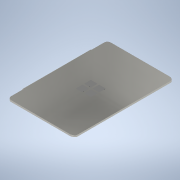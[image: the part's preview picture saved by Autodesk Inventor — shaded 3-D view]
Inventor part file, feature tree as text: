
AUTODESK INVENTOR PART (.ipt)
format: ipt  version: 2022 (Build 260153000, 153)  size: 223,744 bytes
history: native  units: mm
features: extrude x6, sketch x4, plane x1, direct_edit x1, other x1
ambient origin geometry x8: Origin, YZ Plane, XZ Plane, XY Plane, X Axis, Y Axis, Z Axis, Center Point
bodies: Body1 (feature_tree)
feature tree (13):
  plane  "Work Plane1"
  sketch  "Sketch2"  dims[d7=0.5mm d8=0.0mm d9=0.49mm d10=0.0mm]
  extrude  "Extrusion2"  Depth=0.5mm TaperAngle=0.0deg
  extrude  "Extrusion3"  Depth=2.0mm
  extrude  "Extrusion4"  Depth=0.5mm
  extrude  "Extrusion5"  Depth=10.0mm
  extrude  "Extrusion6"  Depth=10.0mm
  extrude  "Extrusion7"  Depth=10.0mm TaperAngle=0.0deg
  direct_edit  "Direct Edit1"
  sketch  "Sketch3"  dims[d11=2.0mm d12=2.0mm]
  sketch  "Sketch4"  dims[d13=0.5mm d14=0.5mm]
  sketch  "Sketch6"  dims[d15=0.5mm d16=12.75mm d17=7.75mm d18=0.001mm d19=0.0mm d20=0.25mm d21=0.315mm d22=15.0mm d23=0.001mm d24=0.0mm d26=0.0mm d32=21.5mm d33=0.0mm d34=20.425mm d35=0.0mm d36=0.5mm d37=5.0mm d38=10.0mm d39=10.0mm]
  other  "Scale1"
